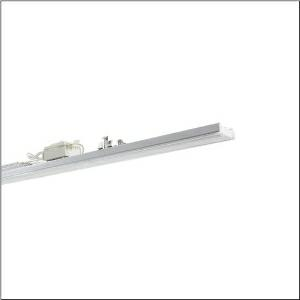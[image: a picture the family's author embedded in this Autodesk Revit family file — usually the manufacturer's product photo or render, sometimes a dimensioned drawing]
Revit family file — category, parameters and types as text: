
# Revit family: licross_21_recessed_mo_52te1edv4e5g
name_source: partatom
category: Lighting Fixtures
units: mm (PartAtom-declared; Revit-internal decimal feet)

## family parameters
Cut with Voids When Loaded = No
Host = Face
Light Source = No
Part Type = Normal
Room Calculation Point = No
Round Connector Dimension = Use Diameter
Shared = No

## types (1)
- --- (1 x LED, 14910 lm, 85.3 W, 4000K)
    Apparent Load = 85 VA
    CIE Flux Codes = 85 95 99 100 100
    Color Rendering = 80
    Color Temperature = 4000K
    Default Elevation = 1800 mm
    Description = Licross 21 Recessed MO, luminaire insert, of sheet steel, galvanised, coil coated, white, length: 2.250mm, width: 66mm, height: 67mm, LED rated luminous flux: 14.910lm, light colour: 840, SDCM (Standard Deviation of Colour Matching)MacAdam ≤ 3 SDCM (initial), control gear: DALI 2, with plug, 5-pole, with phase selection, mains connection: 220..240V, AC, 50/60Hz, rated input power: 85W, internal wiring halogen-free, primary light control with lens, of plastic, primary optical cover: cover, of PMMA, light emission: direct distribution, primary light characteristic: symmetric, protection rating (complete): IP54, insulation class (complete): insulation class I (protective earthing), certification: CE, ENEC, VDE, UKCA, protection symbol: D if used in an environment with non-conductive dust loads with corresponding accessories, impact resistance: IK06, permissible ambient temperature for indoor applications: -25..+35°C, corresponds to IFS (International Featured Standards) requirements for safety and quality in the food industry, reducing of maximum allowable ambient temperature of 5°C with ceiling mounting, LABS conformity tested according to VDMA 24364:2018-05, The light source and the operating device comply with the requirements of the Ecodesign Regulation (EU) 2019/2020 and are replaceable in accordance with this regulation, packaging unit: 1 piece
    Height = 58 mm
    Lamp = 1 x LED
    Lamp Light Flux = 14910 lm
    Lamp Power = 85.3 W
    Lamp count = 1
    Length = 2250 mm
    Luminous efficacy = 175 lm/W
    Manufacturer = Siteco
    ModVariant = No
    Model = 52TE1EDV4E5G
    Mounting Place = Ceiling
    Mounting Type = Pendant
    Number of Poles = 1
    OnlyDefault = Yes
    Power Factor = 1
    Product Name = Licross 21 Recessed MO
    Product group = luminaire insert | ceiling pendant
    ProductGroupID = 901
    Protection Class = Protection class I
    Protection Degree = IP 54
    RLX_Detail_Level = 1
    RLX_Emergency_Light_Flux = 0 lm
    RLX_Emergency_Type = 0
    RLX_Emergency_Type_DB = No
    RlxData = <blob elided: 29921 chars, md5=d6eb1f7a>
    Socket = socket
    Standby Power = 0 W
    System Light Flux = 14910 lm
    System Power = 85 W
    Type Comments = factory setting: luminous flux: 100 % | dim-lin: 254 | 390 mA
    Type Image = l_1296930.jpg
    URL = http://relux.com
    VarID = @adj_125673
    Voltage = 0 V
    Weight = 0.00 kg
    Width = 66 mm

## geometry (parser evidence)
native form markers: Blend x4, Sweep x8
no freeform markers — native parametric forms only
